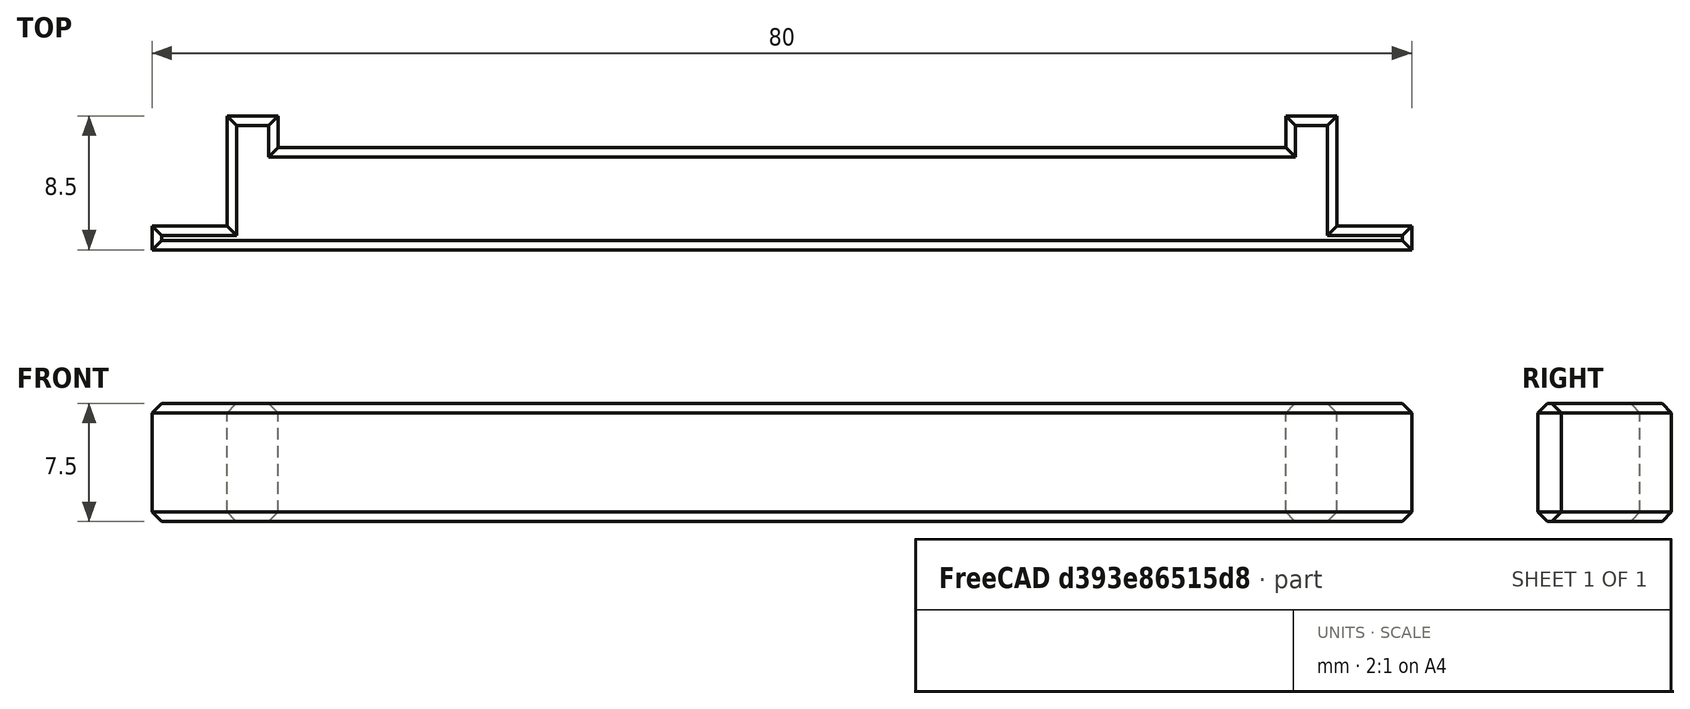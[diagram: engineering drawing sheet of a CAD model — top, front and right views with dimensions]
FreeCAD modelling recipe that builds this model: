
FCSTD DOCUMENT  (FreeCAD 0.18R4 (GitTag))
Label: Bass_Mount
License: All rights reserved
LicenseURL: http://en.wikipedia.org/wiki/All_rights_reserved
objects: Sketcher::SketchObject×1, PartDesign::Pad×1, PartDesign::Chamfer×1, PartDesign::Body×1, Mesh::Feature×1
note: 5 computed .brp shape members not serialized (recipe doc carries the construction recipe); baked Part::Feature solids carry a one-line shape summary decoded from their .brp

FEATURE [Sketcher::SketchObject] Sketch
  MapMode = 5
  Support = -> [XY_Plane]
  sketch-geometry (12):
    g0: LineSegment StartX=-40 StartY=0 StartZ=0 EndX=40 EndY=0 EndZ=0
    g1: LineSegment StartX=40 StartY=0 StartZ=0 EndX=40 EndY=1.5 EndZ=0
    g2: LineSegment StartX=40 StartY=1.5 StartZ=0 EndX=35.25 EndY=1.5 EndZ=0
    g3: LineSegment StartX=35.25 StartY=1.5 StartZ=0 EndX=35.25 EndY=8.5 EndZ=0
    g4: LineSegment StartX=35.25 StartY=8.5 StartZ=0 EndX=32 EndY=8.5 EndZ=0
    g5: LineSegment StartX=32 StartY=8.5 StartZ=0 EndX=32 EndY=6.5 EndZ=0
    g6: LineSegment StartX=32 StartY=6.5 StartZ=0 EndX=-32 EndY=6.5 EndZ=0
    g7: LineSegment StartX=-32 StartY=6.5 StartZ=0 EndX=-32 EndY=8.5 EndZ=0
    g8: LineSegment StartX=-32 StartY=8.5 StartZ=0 EndX=-35.25 EndY=8.5 EndZ=0
    g9: LineSegment StartX=-35.25 StartY=8.5 StartZ=0 EndX=-35.25 EndY=1.5 EndZ=0
    g10: LineSegment StartX=-35.25 StartY=1.5 StartZ=0 EndX=-40 EndY=1.5 EndZ=0
    g11: LineSegment StartX=-40 StartY=1.5 StartZ=0 EndX=-40 EndY=0 EndZ=0
  constraints (33):
    c: PointOnObject(g0,g-1)
    c: Coincident(g0,g1)
    c: Vertical(g1)
    c: Coincident(g1,g2)
    c: Horizontal(g2)
    c: Coincident(g2,g3)
    c: Vertical(g3)
    c: Coincident(g3,g4)
    c: Horizontal(g4)
    c: Coincident(g4,g5)
    c: Vertical(g5)
    c: Coincident(g5,g6)
    c: Coincident(g6,g7)
    c: Vertical(g7)
    c: Coincident(g7,g8)
    c: Horizontal(g8)
    c: Coincident(g8,g9)
    c: Vertical(g9)
    c: Coincident(g9,g10)
    c: Horizontal(g10)
    c: Coincident(g10,g11)
    c: Coincident(g11,g0)
    c: Vertical(g11)
    c: Symmetric(g0,g0,g-2)
    c: Symmetric(g6,g5,g-2)
    c: Symmetric(g8,g3,g-2)
    c: DistanceX(g0,g0) = 80
    c: DistanceY(g1,g1) = 1.5
    c: Equal(g11,g1)
    c: DistanceX(g6,g6) = 64
    c: DistanceY(g5,g3) = 2
    c: DistanceX(g4,g4) = 3.25
    c: DistanceY(g1,g5) = 5
FEATURE [PartDesign::Pad] Pad
  Length = 7.5
  Length2 = 100
  Profile = -> Sketch
  Refine = true
  Type = 0
FEATURE [PartDesign::Chamfer] Chamfer
  Base = -> Pad [Face14,Face13]
  BaseFeature = -> Pad
  Size = 0.6
FEATURE [PartDesign::Body] Body
  Group = -> [Sketch,Pad,Chamfer]
  Origin = -> Origin
  Tip = -> Chamfer
FEATURE [Mesh::Feature] Mesh  label="Chamfer (Meshed)"
